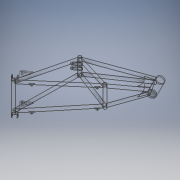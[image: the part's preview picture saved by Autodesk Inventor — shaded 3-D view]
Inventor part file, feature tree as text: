
AUTODESK INVENTOR PART (.ipt)
format: ipt  version: 2019.3 (Build 233278000, 278)  size: 878,080 bytes
history: native  units: mm
features: sketch x22, extrude x20, other x17, plane x15, mirror x6, hole x1, fillet x1, projected_geometry x1
ambient origin geometry x8: Origin, YZ Plane, XZ Plane, XY Plane, X Axis, Y Axis, Z Axis, Center Point
bodies: Body1 (feature_tree), Body2 (feature_tree), Body3 (feature_tree), Body4 (feature_tree), Body5 (feature_tree), Body6 (feature_tree), Body7 (feature_tree), Body8 (feature_tree), Body9 (feature_tree), Body10 (feature_tree), Body11 (feature_tree)
feature tree (83):
  other  "Frame"
  other  "Linkage"
  extrude  "Extrusion2"  Depth=2.0mm
  plane  "Work Plane2"
  plane  "Work Plane54"
  extrude  "Extrusion3"  Depth=3.5mm
  plane  "Work Plane60"
  plane  "Work Plane61"
  extrude  "Extrusion46"  Depth=10.0mm
  extrude  "Extrusion10"  Depth=2.0mm
  extrude  "Extrusion11"  Depth=22.225mm
  plane  "Work Plane11"
  sketch  "3D Sketch3"
  plane  "Work Plane16"
  extrude  "Extrusion12"  Depth=150.0mm TaperAngle=0.0deg
  plane  "Work Plane17"
  sketch  "Sketch19"  dims[d99=14.0mm d100=14.0mm]
  extrude  "Extrusion13"  Depth=14.0mm
  extrude  "Extrusion9"  Depth=2.0mm
  extrude  "Extrusion22"  Depth=22.225mm
  plane  "Work Plane18"
  extrude  "Extrusion14"  Depth=135.0mm TaperAngle=0.0deg
  plane  "Work Plane20"
  extrude  "Extrusion16"  Depth=2.0mm
  plane  "Work Plane21"
  sketch  "Sketch23"  dims[d108=2.0mm d109=135.0mm d110=0.0mm]
  extrude  "Extrusion17"  Depth=17.0mm
  plane  "Work Plane26"
  extrude  "Extrusion18"  Depth=27.0mm
  mirror  "Mirror4"
  mirror  "Mirror3"
  extrude  "Extrusion19"  Depth=22.225mm
  plane  "Work Plane27"
  extrude  "Extrusion23"  Depth=422.0mm TaperAngle=0.0deg
  extrude  "Extrusion24"  Depth=2.0mm
  hole  "Hole1"  [1 undecoded]
  fillet  "Fillet1"  Radius=4.0mm
  extrude  "Extrusion20"  Depth=6.0mm TaperAngle=0.0deg
  mirror  "Mirror5"
  mirror  "Mirror6"
  sketch  "3D Sketch19"
  plane  "Work Plane57"
  extrude  "Extrusion41"  Depth=10.0mm
  mirror  "Mirror11"
  plane  "Work Plane58"
  extrude  "Extrusion42"  Depth=10.0mm TaperAngle=0.0deg
  plane  "Work Plane59"
  extrude  "Extrusion44"  Depth=10.0mm
  mirror  "Mirror12"
  sketch  "Sketch3"  dims[d23=22.225mm d24=2.0mm]
  sketch  "Sketch4"  dims[d25=120.0mm d26=0.0mm d28=3.5mm]
  sketch  "Sketch13"  dims[d29=134.0mm d30=0.0mm d77=10.0mm]
  sketch  "Sketch16"  dims[d78=89.5mm d79=6.0mm d80=0.0mm d90=2.0mm]
  sketch  "Sketch17"  dims[d91=205.75mm d92=0.0mm d94=22.225mm]
  sketch  "Sketch18"  dims[d95=2.0mm d96=150.0mm d97=0.0mm]
  sketch  "Sketch20"  dims[d101=22.225mm d102=2.0mm]
  sketch  "Sketch22"  dims[d105=135.0mm d106=0.0mm d107=22.225mm]
  sketch  "Sketch25"  dims[d111=22.225mm d112=2.0mm]
  other  "PivotPlateRight"
  other  "ShockPlateRight"
  sketch  "Sketch26"  dims[d113=135.0mm d114=0.0mm d115=17.0mm]
  sketch  "Sketch27"  dims[d116=8.0mm d117=27.0mm]
  other  "Pattern of ShockPlateRight:1"
  other  "PivotPlateLeft"
  sketch  "Sketch30"  dims[d118=7.0mm d123=22.225mm]
  sketch  "Sketch31"  dims[d124=2.0mm d125=422.0mm d126=0.0mm]
  other  "FootpegRight"
  sketch  "Sketch32"  dims[d127=22.225mm d128=2.0mm]
  other  "Pattern of ShockPlateRight:2"
  other  "FootpegLeft"
  other  "HeadTube"
  other  "Image2"
  sketch  "Sketch51"  dims[d129=422.0mm d130=0.0mm d132=12.0mm]
  other  "HeadTubeReinforcePlateRight"
  other  "Pattern of ShockPlateRight:5"
  other  "HeadTubeReinforcePlateLeft"
  other  "Pattern of ShockPlateRight:6"
  other  "ShockPlateLeft"
  sketch  "Sketch55"  dims[d133=24.0mm d134=8.0mm d135=24.0mm d140=4.0mm d141=0.0mm]
  other  "BatteryFastenerTabs"
  sketch  "Sketch56"  dims[d143=6.0mm d144=0.0mm d145=6.0mm d146=0.0mm]
  sketch  "Sketch59"  dims[d152=7.0mm d153=10.0mm d154=10.0mm d158=76.75mm d159=0.0mm d160=9.599311mm d161=24.0mm d162=26.5mm d163=4.4mm d164=4.658765mm d165=4.4mm d166=0.0mm d167=24.0mm d168=0.0mm d169=12.5mm d170=8.7mm d171=6.0mm d172=4.0mm d173=2.0mm d174=90.0deg d175=8.0mm d176=20.594885mm d177=10.0mm d217=3.3mm d221=38.1mm d222=44.0mm d224=13.0mm d225=51.0mm d268=3.0mm d269=0.0mm d270=85.0mm d271=6.0mm d273=28.0mm d274=13.0mm d275=4.4mm d276=0.0mm d277=65.0mm d278=6.0mm d279=3.5mm d280=28.0mm d281=13.0mm d284=4.4mm d285=0.0mm d286=3.5mm d287=-10.0mm d288=-10.0mm d289=2.0mm d292=10.0mm d293=0.0mm]
  projected_geometry  "Project Cut Edges10"
note: 1 required parameter value undecoded (feature->parameter linkage not recoverable at this tier; creation-order binding heuristic only, values carry confidence <= 0.55)
